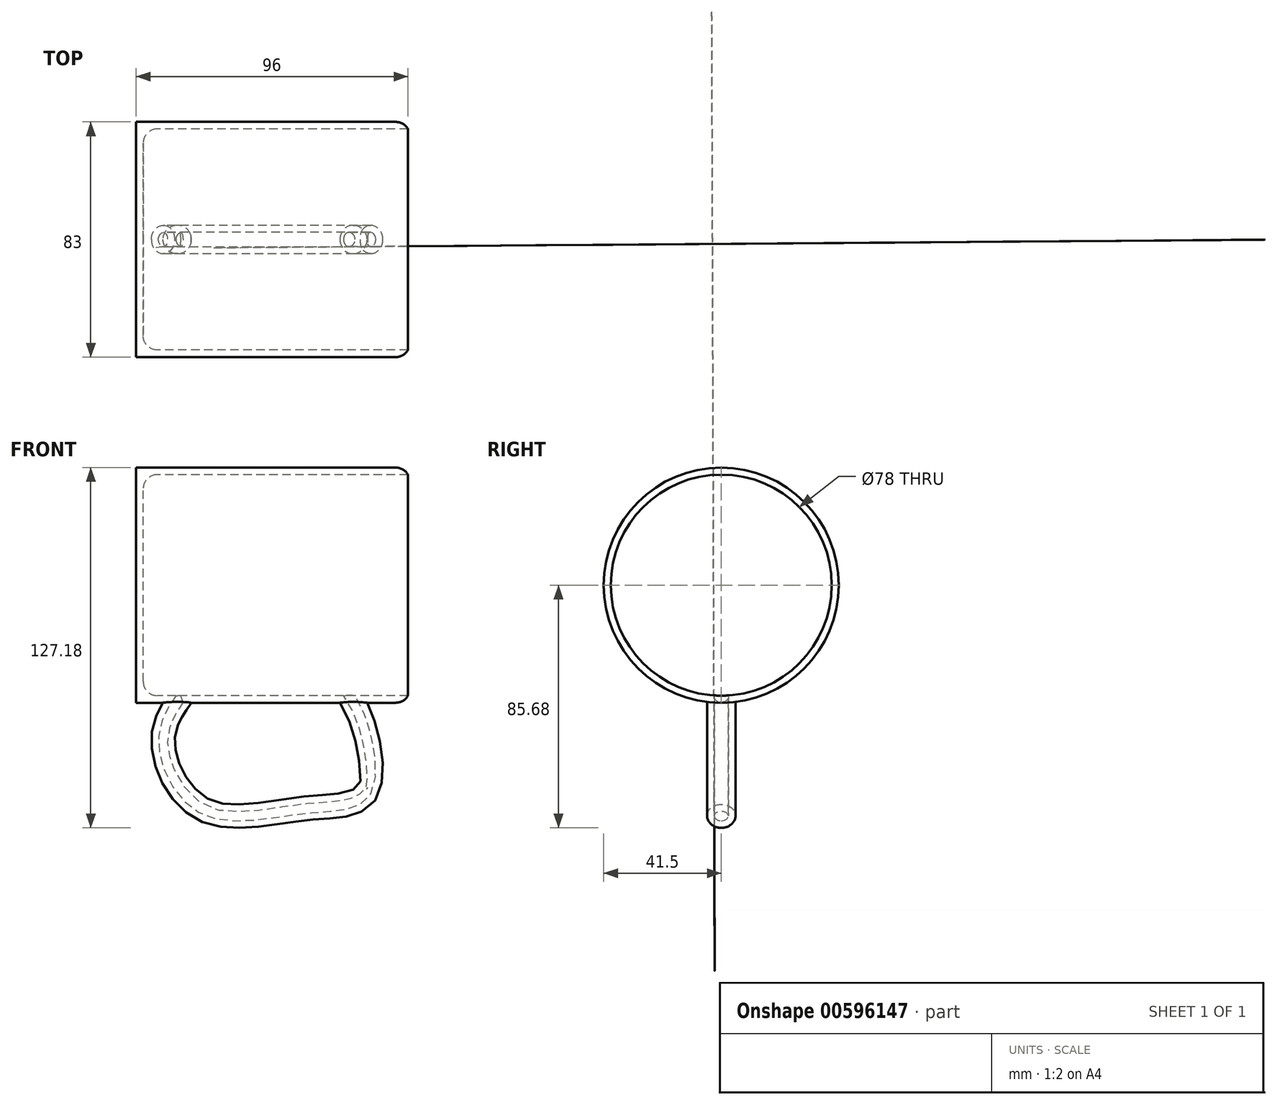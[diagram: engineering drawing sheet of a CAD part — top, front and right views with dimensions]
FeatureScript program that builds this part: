
annotation { "Feature Type Name" : "Feature", "Feature Type Description" : "" }
export const myFeature = defineFeature(function(context is Context, id is Id, definition is map)
    precondition{}
    {
        {
            var Q0;
            Q0=qCreatedBy(makeId("Right.planeOp"),FACE);
            var sketch = newSketch(context, id + "F0", { "sketchPlane" : qUnion([Q0])});
            skCircle(sketch, "E0", {"center": v(0, 0) * mm, "radius": 41.5 * mm});
            skSolve(sketch);
        }
        {
            var Q0;
            Q0 = qSketchRegion(id + "F0", true);
            extrude(context, id + "F1", {"entities" : qUnion([Q0]), "depth" : 96 * mm, "offsetDistance" : 25 * mm});
        }
        {
            var Q0;
            Q0=qCreatedBy(makeId("Front.planeOp"),FACE);
            var sketch = newSketch(context, id + "F2", { "sketchPlane" : qUnion([Q0])});
            skFitSpline(sketch, "E1", {"points": [v(17.34, -36.39) * mm, v(9.07, -54.93) * mm, v(23.44, -79.5) * mm, v(60.5, -79.35) * mm, v(82.24, -72.04) * mm, v(74.63, -37.55) * mm, v(65, -35.49) * mm], "startDerivative": vector(-81.37, -110.48) * mm, "endDerivative": vector(-92.75, -16.71) * mm});
            skSolve(sketch);
        }
        {
            var Q0;
            Q0=qCreatedBy(makeId("Top.planeOp"),FACE);
            cPlane(context, id + "F3", {"entities" : qUnion([Q0]), "cplaneType" : CPlaneType.OFFSET, "offset" : 40 * mm, "oppositeDirection" : true, "width" : 150 * mm, "height" : 150 * mm});
        }
        {
            var Q0;
            Q0=qCreatedBy(id+"F3.planeOp",FACE);
            var sketch = newSketch(context, id + "F4", { "sketchPlane" : qUnion([Q0])});
            skCircle(sketch, "E2", {"center": v(75.8, 0) * mm, "radius": 5 * mm});
            skSolve(sketch);
        }
        {
            var Q0;
            Q0 = qSketchRegion(id + "F4", true);
            var Q1;
            Q1 = qConstructionFilter(qBodyType(qCreatedBy(id + "F2" ,EDGE), BodyType.WIRE), ConstructionObject.NO);
            sweep(context, id + "F5", {"operationType" : NewBodyOperationType.ADD, "profiles" : qUnion([Q0]), "path" : qUnion([Q1])});
        }
        {
            var Q0;
            Q0=makeQuery(id+"F1.opExtrude","CAP_FACE",FACE,{"disambiguationData":[OSD([sQuery(id+"F0.wireOp",EDGE,"E0")])],"isStart":false});
            shell(context, id + "F6", {"entities" : qUnion([Q0]), "thickness" : 2.5 * mm});
        }
        {
            var Q0;
            Q0=makeQuery(id+"F1.opExtrude","CAP_EDGE",EDGE,{"disambiguationData":[OSD([sQuery(id+"F0.wireOp",EDGE,"E0")])],"isStart":false});
            fillet(context, id + "F7", {"entities" : qUnion([Q0]), "radius" : 5 * mm, "tangentPropagation" : true, "allowEdgeOverflow" : false});
        }
        {
            var Q0;
            {var subQ0=sQuery(id+"F0.wireOp",EDGE,"E0");Q0=makeQuery(id+"F6.opShell","OFFSET_EDGE",EDGE,{"disambiguationData":[OSD([subQ0]),TDD([makeQuery(id+"F1.opExtrude","CAP_EDGE",EDGE,{"disambiguationData":[OSD([subQ0])],"isStart":true})])]});}
            fillet(context, id + "F8", {"entities" : qUnion([Q0]), "radius" : 5 * mm, "tangentPropagation" : true, "allowEdgeOverflow" : false});
        }
    });
